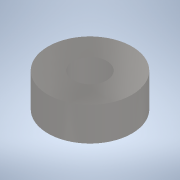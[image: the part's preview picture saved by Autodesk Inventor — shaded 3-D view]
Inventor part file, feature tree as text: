
AUTODESK INVENTOR PART (.ipt)
format: ipt  version: 2022 (Build 260153000, 153)  size: 98,304 bytes
history: native  units: in
note: dims shown in document units (in); Inventor stores cm internally (conversion verified against a paired STEP export)
features: extrude x1, sketch x1
ambient origin geometry x8: Origin, YZ Plane, XZ Plane, XY Plane, X Axis, Y Axis, Z Axis, Center Point
bodies: Solid1 (feature_tree)
feature tree (2):
  extrude  "Extrusion1"  Depth=0.3937in
  sketch  "Sketch1"  dims[d0=0.1575in d1=0.3937in d2=0.1575in d3=0.0in]
